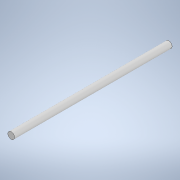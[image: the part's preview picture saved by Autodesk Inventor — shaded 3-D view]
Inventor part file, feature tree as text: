
AUTODESK INVENTOR PART (.ipt)
format: ipt  version: 2021 (Build 250183000, 183)  size: 91,648 bytes
history: native  units: mm
features: extrude x1, sketch x1
ambient origin geometry x8: Origin, YZ Plane, XZ Plane, XY Plane, X Axis, Y Axis, Z Axis, Center Point
bodies: Solid1 (feature_tree)
feature tree (2):
  extrude  "Extrusion1"  Depth=71.0mm TaperAngle=0.0deg
  sketch  "Sketch1"  dims[d0=3.0mm d1=71.0mm d2=0.0mm]
